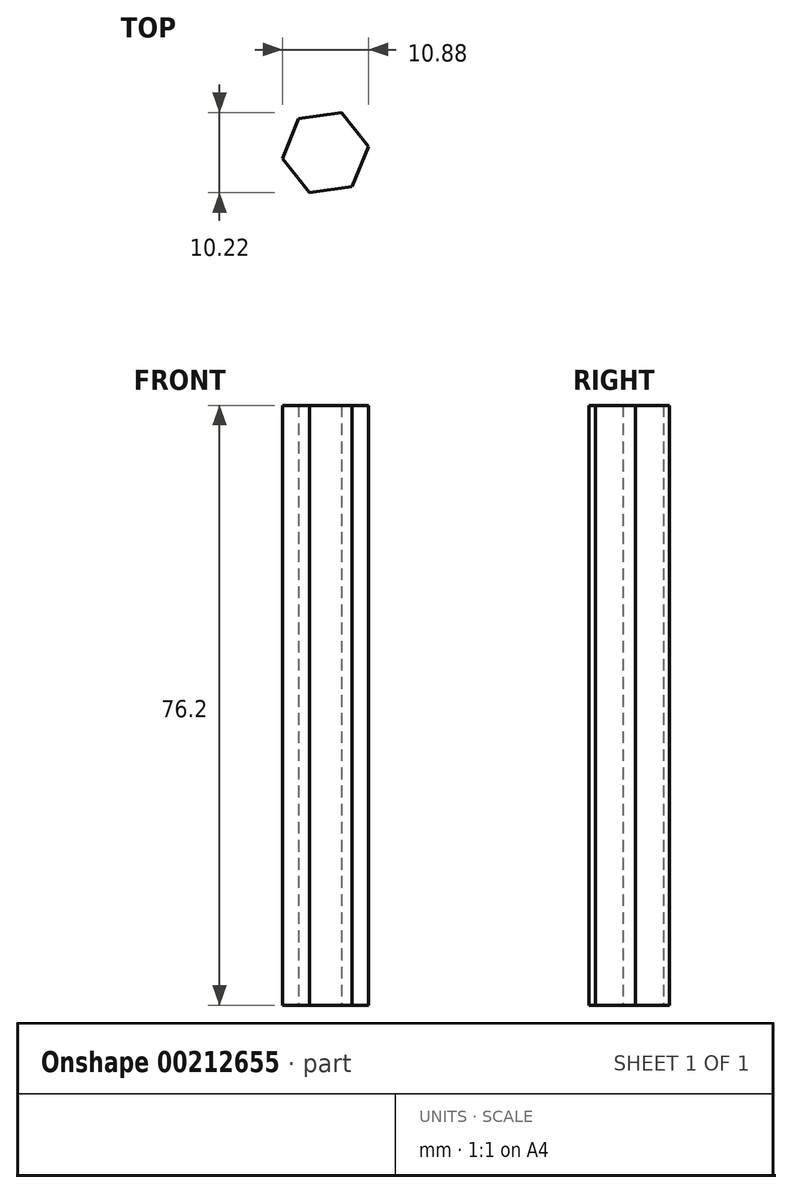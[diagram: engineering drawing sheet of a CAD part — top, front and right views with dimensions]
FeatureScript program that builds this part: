
annotation { "Feature Type Name" : "Feature", "Feature Type Description" : "" }
export const myFeature = defineFeature(function(context is Context, id is Id, definition is map)
    precondition{}
    {
        {
            var Q0;
            Q0=qCreatedBy(makeId("Top.planeOp"),FACE);
            var sketch = newSketch(context, id + "F0", { "sketchPlane" : qUnion([Q0])});
            skCircle(sketch, "E0.cCircle", {"center": v(0, 0) * mm, "radius": 4.76 * mm, "construction": true});
            skLineSegment(sketch, "E0.0", {"start": v(-3.4, 4.32) * mm, "end": v(2.04, 5.1) * mm});
            skLineSegment(sketch, "E0.1", {"start": v(2.04, 5.1) * mm, "end": v(5.44, 0.79) * mm});
            skLineSegment(sketch, "E0.2", {"start": v(5.44, 0.79) * mm, "end": v(3.4, -4.32) * mm});
            skLineSegment(sketch, "E0.3", {"start": v(3.4, -4.32) * mm, "end": v(-2.04, -5.1) * mm});
            skLineSegment(sketch, "E0.4", {"start": v(-2.04, -5.1) * mm, "end": v(-5.44, -0.79) * mm});
            skLineSegment(sketch, "E0.5", {"start": v(-5.44, -0.79) * mm, "end": v(-3.4, 4.32) * mm});
            skPoint(sketch, "E0.0.midPoint", {"position": v(-0.68, 4.71) * mm});
            skSolve(sketch);
        }
        {
            var Q0;
            Q0=makeQuery(id+"F0.imprint","IMPRINT",FACE,{"disambiguationData":[TD([[makeQuery(id+"F0.imprint","IMPRINT",EDGE,{"derivedFrom":sQuery(id+"F0.wireOp",EDGE,"E0.0")}),-1.0]])]});
            extrude(context, id + "F1", {"entities" : qUnion([Q0]), "depth" : 76.2 * mm});
        }
    });
